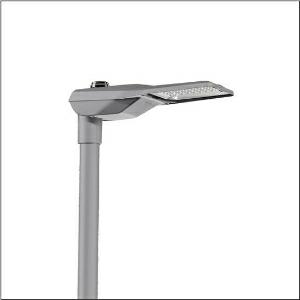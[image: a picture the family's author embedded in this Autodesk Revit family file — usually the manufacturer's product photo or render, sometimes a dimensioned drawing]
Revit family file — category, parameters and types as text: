
# Revit family: streetlight_sl_21_mini___st1_0a_5xe6d47n08jb_8270
name_source: partatom
category: Lighting Fixtures
units: mm (PartAtom-declared; Revit-internal decimal feet)

## family parameters
Cut with Voids When Loaded = No
Host = Face
Light Source = No
Part Type = Normal
Room Calculation Point = No
Round Connector Dimension = Use Diameter
Shared = No

## types (1)
- --- (1 x LED, 13390 lm, 87.3 W, 4000K)
    Apparent Load = 87 VA
    CIE Flux Codes = 40 73 97 100 100
    Color Rendering = 70
    Color Temperature = 4000K
    Default Elevation = 1800 mm
    Description = Streetlight SL 21 mini, mast luminaire, primary light control with lens, of PMMA, primary optical cover: cover, of toughened safety glass, transparent, light distribution: ST1.0a, light emission: direct distribution, primary light characteristic: asymmetric, installation type: side-entry, LED, 3G 2.5mm², High Power LED, rated luminous flux: 13.390lm, luminous efficacy: 153lm/W, light colour: 740, colour temperature: 4000K, control gear: NEMA (7pin), control: overheat protection, pre-setting: linear dimming characteristic, constant luminous flux control, time-dependent luminous flux control, flexible luminous flux parameterisation, mains connection: 230..240V, AC, 50/60Hz, connection cable pre-assembled, cable length: 10,5m, wiring characteristics: H05VV-F, start of lifetime: 87W, end of service life: 90W, reduction: 40W, luminaire housing, of diecast aluminium (EN AC-44300), powder-coated, SITECO metallic grey (DB 702S), corrosivity category C5 high according to DIN EN ISO 12944, multi-level sealing system, sealing non-destructively replaceable, inclination adjustable: 0°, 5°, 10°, 15°, length: 628mm, width: 235mm, height: 110mm, spigot size: 42mm (side-entry), mounting height: 4..8m, protection rating (complete): IP66, insulation class (complete): insulation class I (protective earthing), certification: CE, ENEC, ENEC+, VDE, impact resistance: IK10, permissible operating ambient temperature for outdoor applications: -40..+50°C, standard-compliant lighting for roads and squares, packaging unit: 1 piece

Light Distribution: ST1.0a
    Height = 110 mm
    Lamp = 1 x LED
    Lamp Light Flux = 13390 lm
    Lamp Power = 87.3 W
    Lamp count = 1
    Length = 625 mm
    Luminous efficacy = 153 lm/W
    Manufacturer = Siteco
    ModVariant = No
    Model = 5XE6D47N08JB
    Number of Poles = 1
    OnlyDefault = Yes
    Power Factor = 1
    Product Name = Streetlight SL 21 mini | ST1.0a
    Product group = mast luminaire | pylon top
    ProductGroupID = 6100
    Protection Class = Protection class I
    Protection Degree = IP 66
    RLX_Detail_Level = 1
    RLX_Emergency_Light_Flux = 0 lm
    RLX_Emergency_Type = 0
    RLX_Emergency_Type_DB = No
    RlxData = <blob elided: 26069 chars, md5=94313584>
    Socket = socket
    Standby Power = 0 W
    System Light Flux = 13390 lm
    System Power = 87 W
    Type Comments = factory setting: luminous flux: 100 % | dim-lin: 254 | 915 mA
    Type Image = l_1294379.jpg
    URL = http://relux.com
    VarID = @adj_134817
    Voltage = 0 V
    Weight = 0.00 kg
    Width = 234 mm

## geometry (parser evidence)
native form markers: Blend x4, Sweep x10
no freeform markers — native parametric forms only
